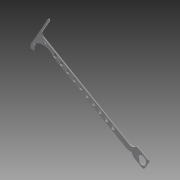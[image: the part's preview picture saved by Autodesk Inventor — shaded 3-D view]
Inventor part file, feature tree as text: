
AUTODESK INVENTOR PART (.ipt)
format: ipt  version: 2013 (Build 170138000, 138)  size: 215,040 bytes
history: native  units: in
note: dims shown in document units (in); Inventor stores cm internally (conversion verified against a paired STEP export)
features: fillet x10, extrude x8, sketch x8, reference x2
ambient origin geometry x8: Origin, YZ Plane, XZ Plane, XY Plane, X Axis, Y Axis, Z Axis, Center Point
bodies: Solid1 (feature_tree)
feature tree (28):
  extrude  "Extrusion1"  Depth=0.75in
  fillet  "Fillet1"  [1 undecoded]
  extrude  "Extrusion2"  Depth=13.325in
  fillet  "Fillet2"  Radius=0.75in
  fillet  "Fillet3"  Radius=1.125in
  extrude  "Extrusion5"  Depth=2.0in
  extrude  "Extrusion6"  Depth=0.75in
  fillet  "Fillet4"  Radius=0.75in
  fillet  "Fillet5"  Radius=0.5in
  extrude  "Extrusion7"  Depth=0.5in
  extrude  "Extrusion8"  Depth=0.375in
  fillet  "Fillet6"  Radius=0.5in
  extrude  "Extrusion9"  Depth=1.0in TaperAngle=0.0deg
  fillet  "Fillet7"  Radius=0.25in
  fillet  "Fillet8"  Radius=0.25in
  fillet  "Fillet9"  Radius=0.5in
  fillet  "Fillet10"  Radius=2.5in
  extrude  "Extrusion10"  Depth=0.125in TaperAngle=0.0deg
  sketch  "Sketch1"  dims[d0=2.8284in d1=0.75in d3=30.0deg]
  sketch  "Sketch2"  dims[d4=14.0in d5=13.325in d6=0.75in d7=1.125in]
  sketch  "Sketch7"  dims[d9=1.5in d10=2.0in]
  sketch  "Sketch8"  dims[d11=0.75in d12=0.75in d13=0.75in d14=0.5in]
  sketch  "Sketch9"  dims[d15=0.125in d16=0.0in d17=0.5in]
  sketch  "Sketch10"  dims[d18=0.125in d19=0.375in d20=0.5in]
  reference  "Reference1"
  reference  "Reference2"
  sketch  "Sketch11"  dims[d21=5.1181in d23=1.0in d24=0.3937in d26=1.0in d28=1.0in d29=0.0in d30=0.25in d31=0.25in d32=0.5in d42=2.5in]
  sketch  "Sketch12"  dims[d43=0.25in d44=0.125in d45=0.0in d46=0.25in d47=1.125in d48=0.25in d49=0.25in d50=0.0in d51=0.5in d52=0.125in d53=0.125in d54=0.0in d55=0.25in d56=0.0in d57=0.125in d58=0.125in d59=0.25in d60=0.0in d61=0.75in d62=0.75in d63=0.75in d64=0.125in d65=0.25in d66=0.0in]
note: 1 required parameter value undecoded (feature->parameter linkage not recoverable at this tier; creation-order binding heuristic only, values carry confidence <= 0.55)
